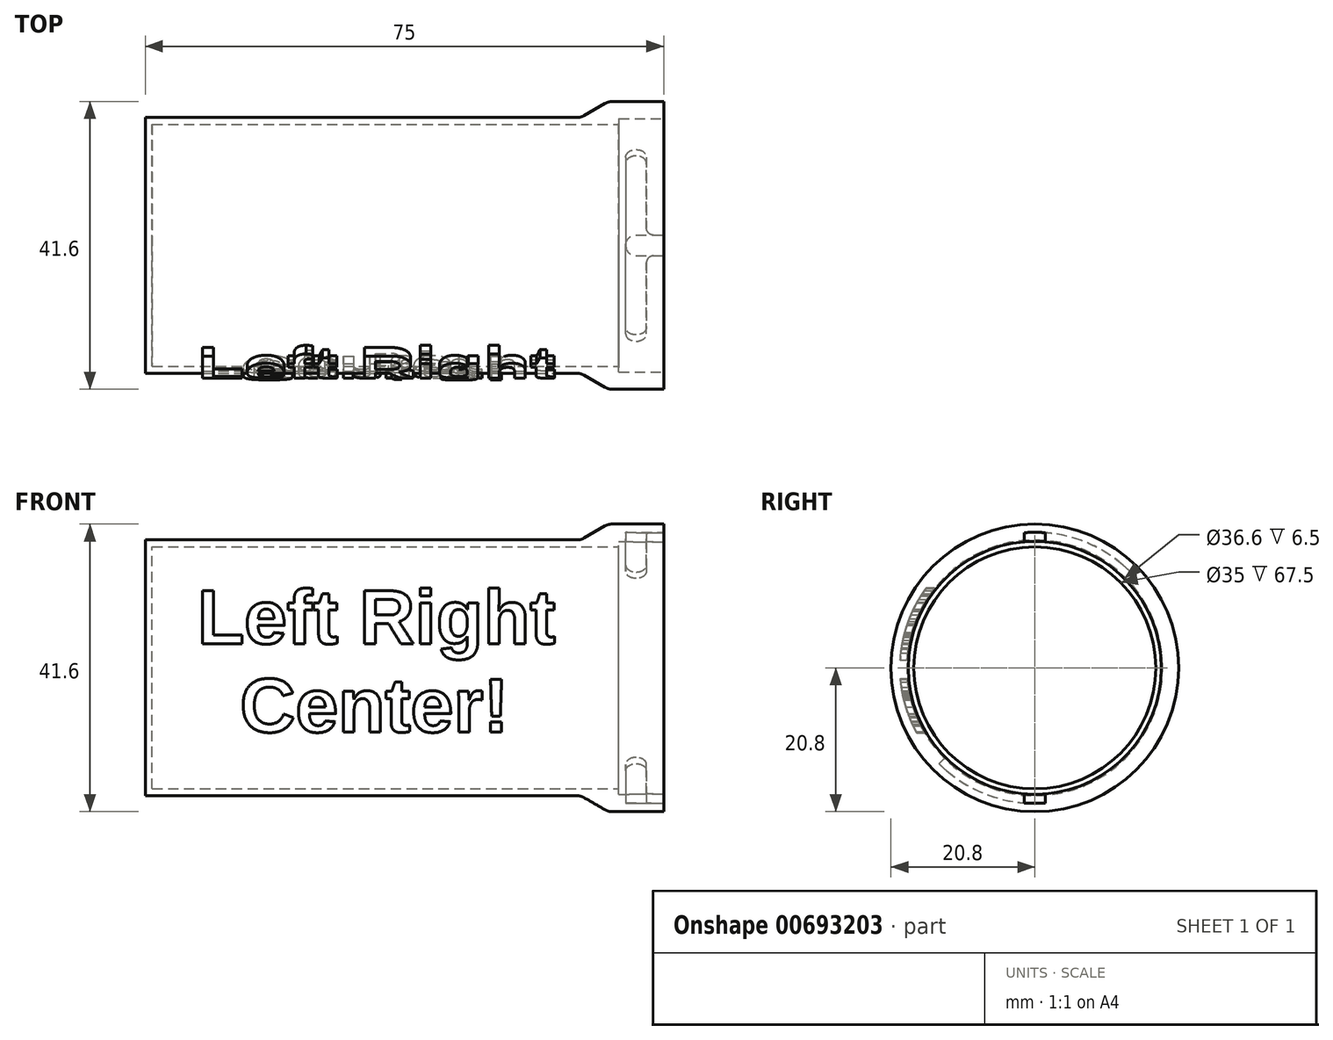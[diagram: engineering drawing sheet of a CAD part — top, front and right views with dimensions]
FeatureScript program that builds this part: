
annotation { "Feature Type Name" : "Feature", "Feature Type Description" : "" }
export const myFeature = defineFeature(function(context is Context, id is Id, definition is map)
    precondition{}
    {
        {
            var Q0;
            Q0=qCreatedBy(makeId("Front.planeOp"),FACE);
            var sketch = newSketch(context, id + "F0", { "sketchPlane" : qUnion([Q0])});
            skLineSegment(sketch, "E0", {"start": v(0, 0) * mm, "end": v(0, 18.5) * mm});
            skLineSegment(sketch, "E1", {"start": v(0, 18.5) * mm, "end": v(63.02, 18.5) * mm});
            skLineSegment(sketch, "E2", {"start": v(67, 20.8) * mm, "end": v(75, 20.8) * mm});
            skLineSegment(sketch, "E3", {"start": v(75, 20.8) * mm, "end": v(75, 18.3) * mm});
            skLineSegment(sketch, "E4", {"start": v(68.5, 17.5) * mm, "end": v(1, 17.5) * mm});
            skLineSegment(sketch, "E5", {"start": v(1, 17.5) * mm, "end": v(1, 0) * mm});
            skLineSegment(sketch, "E6", {"start": v(1, 0) * mm, "end": v(0, 0) * mm});
            skLineSegment(sketch, "E7", {"start": v(68.5, 17.5) * mm, "end": v(68.5, 18.3) * mm});
            skLineSegment(sketch, "E8", {"start": v(68.5, 18.3) * mm, "end": v(75, 18.3) * mm});
            skLineSegment(sketch, "E9", {"start": v(67, 20.8) * mm, "end": v(63.02, 18.5) * mm});
            skSolve(sketch);
        }
        {
            var Q0;
            Q0=makeQuery(id+"F0.imprint","IMPRINT",FACE,{"disambiguationData":[TD([[makeQuery(id+"F0.imprint","IMPRINT",EDGE,{"derivedFrom":sQuery(id+"F0.wireOp",EDGE,"E0")}),-1.0]])]});
            var Q1;
            Q1=sQuery(id+"F0.wireOp",EDGE,"E6");
            revolve(context, id + "F1", {"surfaceOperationType" : NewSurfaceOperationType.NEW, "entities" : qUnion([Q0]), "axis" : qUnion([Q1]), "revolveType" : RevolveType.FULL});
        }
        {
            var Q0;
            Q0=makeQuery(id+"F1.opRevolve","SWEPT_EDGE",EDGE,{"disambiguationData":[OSD([sQuery(id+"F0.wireOp",EDGE,"E2"),sQuery(id+"F0.wireOp",EDGE,"E9")])]});
            var Q1;
            Q1=makeQuery(id+"F1.opRevolve","SWEPT_EDGE",EDGE,{"disambiguationData":[OSD([sQuery(id+"F0.wireOp",EDGE,"E1"),sQuery(id+"F0.wireOp",EDGE,"E9")])]});
            fillet(context, id + "F2", {"entities" : qUnion([Q0, Q1]), "radius" : 2 * mm, "tangentPropagation" : true, "allowEdgeOverflow" : false});
        }
        {
            var Q0;
            Q0=makeQuery(id+"F1.opRevolve","SWEPT_FACE",FACE,{"disambiguationData":[OSD([sQuery(id+"F0.wireOp",EDGE,"E3")])]});
            var sketch = newSketch(context, id + "F3", { "sketchPlane" : qUnion([Q0])});
            skLineSegment(sketch, "E10.left", {"start": v(1.5, 19.54) * mm, "end": v(1.5, -19.54) * mm});
            skLineSegment(sketch, "E10.right", {"start": v(-1.5, 19.54) * mm, "end": v(-1.5, -19.54) * mm});
            skPoint(sketch, "E10.middle", {"position": v(0, 0) * mm});
            skArc(sketch, "E11", {"start": v(1.5, 19.54) * mm, "mid": v(0, 19.6) * mm, "end": v(-1.5, 19.54) * mm});
            skArc(sketch, "E12.trimOffspring", {"start": v(-1.5, -19.54) * mm, "mid": v(0, -19.6) * mm, "end": v(1.5, -19.54) * mm});
            skSolve(sketch);
        }
        {
            var Q0;
            Q0 = qSketchRegion(id + "F3", true);
            extrude(context, id + "F4", {"entities" : qUnion([Q0]), "operationType" : NewBodyOperationType.REMOVE, "oppositeDirection" : true, "depth" : 5.5 * mm, "offsetDistance" : 25 * mm});
        }
        {
            var Q0;
            Q0=qCreatedBy(makeId("Front.planeOp"),FACE);
            var sketch = newSketch(context, id + "F5", { "sketchPlane" : qUnion([Q0])});
            skLineSegment(sketch, "E13.bottom", {"start": v(72.5, 19.6) * mm, "end": v(69.5, 19.6) * mm});
            skLineSegment(sketch, "E13.left", {"start": v(72.5, 19.6) * mm, "end": v(72.5, 0) * mm});
            skLineSegment(sketch, "E13.right", {"start": v(69.5, 19.6) * mm, "end": v(69.5, 0) * mm});
            skPoint(sketch, "E13.middle", {"position": v(74.25, 0) * mm});
            skLineSegment(sketch, "E14", {"start": v(69.5, 0) * mm, "end": v(72.5, 0) * mm, "construction": true});
            skLineSegment(sketch, "E15", {"start": v(69.5, 12.25) * mm, "end": v(72.5, 12.25) * mm});
            skSolve(sketch);
        }
        {
            var Q0;
            {var subQ0=sQuery(id+"F5.wireOp",EDGE,"E13.bottom");Q0=makeQuery(id+"F5.imprint","IMPRINT",FACE,{"disambiguationData":[TD([[makeQuery(id+"F5.imprint","IMPRINT",EDGE,{"derivedFrom":subQ0}),1.0]])]});}
            var Q1;
            Q1=sQuery(id+"F5.wireOp",EDGE,"E14");
            revolve(context, id + "F6", {"operationType" : NewBodyOperationType.REMOVE, "surfaceOperationType" : NewSurfaceOperationType.NEW, "entities" : qUnion([Q0]), "axis" : qUnion([Q1]), "revolveType" : RevolveType.ONE_DIRECTION, "oppositeDirection" : true, "angle" : 45 * degree});
        }
        {
            var Q0;
            Q0=qCreatedBy(makeId("Front.planeOp"),FACE);
            var sketch = newSketch(context, id + "F7", { "sketchPlane" : qUnion([Q0])});
            skLineSegment(sketch, "E16.bottom", {"start": v(72.5, -19.6) * mm, "end": v(69.5, -19.6) * mm});
            skLineSegment(sketch, "E16.top", {"start": v(72.5, 0) * mm, "end": v(69.5, 0) * mm, "construction": true});
            skLineSegment(sketch, "E16.left", {"start": v(72.5, -19.6) * mm, "end": v(72.5, 0) * mm});
            skLineSegment(sketch, "E16.right", {"start": v(69.5, -19.6) * mm, "end": v(69.5, 0) * mm});
            skLineSegment(sketch, "E17", {"start": v(72.5, -11.28) * mm, "end": v(69.5, -11.28) * mm});
            skSolve(sketch);
        }
        {
            var Q0;
            {var subQ0=sQuery(id+"F7.wireOp",EDGE,"E16.bottom");Q0=makeQuery(id+"F7.imprint","IMPRINT",FACE,{"disambiguationData":[TD([[makeQuery(id+"F7.imprint","IMPRINT",EDGE,{"derivedFrom":subQ0}),-1.0]])]});}
            var Q1;
            Q1=sQuery(id+"F7.wireOp",EDGE,"E16.top");
            revolve(context, id + "F8", {"operationType" : NewBodyOperationType.REMOVE, "surfaceOperationType" : NewSurfaceOperationType.NEW, "entities" : qUnion([Q0]), "axis" : qUnion([Q1]), "revolveType" : RevolveType.ONE_DIRECTION, "angle" : 45 * degree});
        }
        {
            var Q0;
            {var subQ0=sQuery(id+"F3.wireOp",EDGE,"E10.right");var subQ1=sQuery(id+"F3.wireOp",EDGE,"E11");Q0=makeQuery(id+"F4.boolean.opBoolean","COPY",EDGE,{"disambiguationData":[TD([makeQuery(id+"F4.opExtrude","SWEPT_FACE",FACE,{"disambiguationData":[OSD([subQ1])]})])],"derivedFrom":makeQuery(id+"F4.opExtrude","CAP_EDGE",EDGE,{"disambiguationData":[OSD([subQ0])],"isStart":false})});}
            var Q1;
            {var subQ0=sQuery(id+"F3.wireOp",EDGE,"E10.left");var subQ1=sQuery(id+"F3.wireOp",EDGE,"E12.trimOffspring");Q1=makeQuery(id+"F4.boolean.opBoolean","COPY",EDGE,{"disambiguationData":[TD([makeQuery(id+"F4.opExtrude","SWEPT_FACE",FACE,{"disambiguationData":[OSD([subQ1])]})])],"derivedFrom":makeQuery(id+"F4.opExtrude","CAP_EDGE",EDGE,{"disambiguationData":[OSD([subQ0])],"isStart":false})});}
            fillet(context, id + "F9", {"entities" : qUnion([Q0, Q1]), "radius" : 1.5 * mm, "tangentPropagation" : true, "allowEdgeOverflow" : false});
        }
        {
            var Q0;
            Q0=makeQuery(id+"F6.boolean.opBoolean","COPY",EDGE,{"derivedFrom":makeQuery(id+"F6.opRevolve","CAP_EDGE",EDGE,{"disambiguationData":[OSD([sQuery(id+"F5.wireOp",EDGE,"E13.right")])],"isStart":false})});
            var Q1;
            Q1=makeQuery(id+"F6.boolean.opBoolean","COPY",EDGE,{"derivedFrom":makeQuery(id+"F6.opRevolve","CAP_EDGE",EDGE,{"disambiguationData":[OSD([sQuery(id+"F5.wireOp",EDGE,"E13.left")])],"isStart":false})});
            var Q2;
            Q2=makeQuery(id+"F8.boolean.opBoolean","COPY",EDGE,{"derivedFrom":makeQuery(id+"F8.opRevolve","CAP_EDGE",EDGE,{"disambiguationData":[OSD([sQuery(id+"F7.wireOp",EDGE,"E16.right")])],"isStart":false})});
            var Q3;
            Q3=makeQuery(id+"F8.boolean.opBoolean","COPY",EDGE,{"derivedFrom":makeQuery(id+"F8.opRevolve","CAP_EDGE",EDGE,{"disambiguationData":[OSD([sQuery(id+"F7.wireOp",EDGE,"E16.left")])],"isStart":false})});
            fillet(context, id + "F10", {"entities" : qUnion([Q0, Q1, Q2, Q3]), "radius" : 1.5 * mm, "tangentPropagation" : true, "allowEdgeOverflow" : false});
        }
        {
            var Q0;
            {var subQ0=sQuery(id+"F3.wireOp",EDGE,"E11");var subQ1=sQuery(id+"F3.wireOp",EDGE,"E10.left");Q0=makeQuery(id+"F6.boolean.opBoolean","INTERSECT",EDGE,{"derivedFrom":[makeQuery(id+"F4.boolean.opBoolean","COPY",FACE,{"disambiguationData":[TD([makeQuery(id+"F4.opExtrude","SWEPT_FACE",FACE,{"disambiguationData":[OSD([subQ0])]})])],"derivedFrom":makeQuery(id+"F4.opExtrude","SWEPT_FACE",FACE,{"disambiguationData":[OSD([subQ1])]})}),makeQuery(id+"F6.opRevolve","SWEPT_FACE",FACE,{"disambiguationData":[OSD([sQuery(id+"F5.wireOp",EDGE,"E13.left")])]})]});}
            var Q1;
            {var subQ0=sQuery(id+"F3.wireOp",EDGE,"E12.trimOffspring");var subQ1=sQuery(id+"F3.wireOp",EDGE,"E10.right");Q1=makeQuery(id+"F8.boolean.opBoolean","INTERSECT",EDGE,{"derivedFrom":[makeQuery(id+"F4.boolean.opBoolean","COPY",FACE,{"disambiguationData":[TD([makeQuery(id+"F4.opExtrude","SWEPT_FACE",FACE,{"disambiguationData":[OSD([subQ0])]})])],"derivedFrom":makeQuery(id+"F4.opExtrude","SWEPT_FACE",FACE,{"disambiguationData":[OSD([subQ1])]})}),makeQuery(id+"F8.opRevolve","SWEPT_FACE",FACE,{"disambiguationData":[OSD([sQuery(id+"F7.wireOp",EDGE,"E16.left")])]})]});}
            fillet(context, id + "F11", {"entities" : qUnion([Q0, Q1]), "radius" : 1 * mm, "tangentPropagation" : true, "allowEdgeOverflow" : false});
        }
        {
            var Q0;
            Q0=qCreatedBy(makeId("Right.planeOp"),FACE);
            var sketch = newSketch(context, id + "F12", { "sketchPlane" : qUnion([Q0])});
            skLineSegment(sketch, "E18", {"start": v(0, 19.88) * mm, "end": v(0, -19.8) * mm});
            skLineSegment(sketch, "E19", {"start": v(0, 19.88) * mm, "end": v(29.27, 19.88) * mm});
            skLineSegment(sketch, "E20", {"start": v(29.27, 19.88) * mm, "end": v(29.27, -21.23) * mm});
            skLineSegment(sketch, "E21", {"start": v(29.27, -21.23) * mm, "end": v(0, -19.8) * mm});
            skSolve(sketch);
        }
        {
            var Q0;
            Q0=qCreatedBy(makeId("Front.planeOp"),FACE);
            var sketch = newSketch(context, id + "F13", { "sketchPlane" : qUnion([Q0])});
            skText(sketch, "E22", { "text": "Left Right \n  Center!", "fontName": "Arimo-Bold.ttf"});
            skLineSegment(sketch, "E23", {"start": v(33.76, 3.5) * mm, "end": v(33.76, 0) * mm, "construction": true});
            skLineSegment(sketch, "E24", {"start": v(7.53, 7.5) * mm, "end": v(0, 7.5) * mm});
            skLineSegment(sketch, "E25", {"start": v(60, 7.5) * mm, "end": v(75, 7.5) * mm});
            const initialGuessF13  = {"E22": [0.00753, 0.0035, 1, 0, 0.008]};
            skSetInitialGuess(sketch, initialGuessF13);
            skSolve(sketch);
        }
        {
            var Q0;
            Q0 = qSketchRegion(id + "F13", true);
            extrude(context, id + "F14", {"entities" : qUnion([Q0]), "operationType" : NewBodyOperationType.ADD, "depth" : 20 * mm, "offsetDistance" : 25 * mm});
        }
        {
            var Q0;
            Q0=makeQuery(id+"F1.opRevolve","SWEPT_FACE",FACE,{"disambiguationData":[OSD([sQuery(id+"F0.wireOp",EDGE,"E0")])]});
            var sketch = newSketch(context, id + "F15", { "sketchPlane" : qUnion([Q0])});
            skCircle(sketch, "E26.0", {"center": v(0, 0) * mm, "radius": 19.5 * mm});
            skCircle(sketch, "E27.0", {"center": v(0, 0) * mm, "radius": 24.5 * mm});
            skSolve(sketch);
        }
        {
            var Q0;
            Q0 = qSketchRegion(id + "F15", true);
            extrude(context, id + "F16", {"entities" : qUnion([Q0]), "operationType" : NewBodyOperationType.REMOVE, "oppositeDirection" : true, "depth" : 61.2 * mm, "offsetDistance" : 25 * mm});
        }
        {
            var Q0;
            Q0=makeQuery(id+"F1.opRevolve","SWEPT_FACE",FACE,{"disambiguationData":[OSD([sQuery(id+"F0.wireOp",EDGE,"E5")])]});
            extrude(context, id + "F17", {"entities" : qUnion([Q0]), "operationType" : NewBodyOperationType.REMOVE, "endBound" : BoundingType.THROUGH_ALL, "depth" : 25 * mm, "offsetDistance" : 25 * mm});
        }
    });
